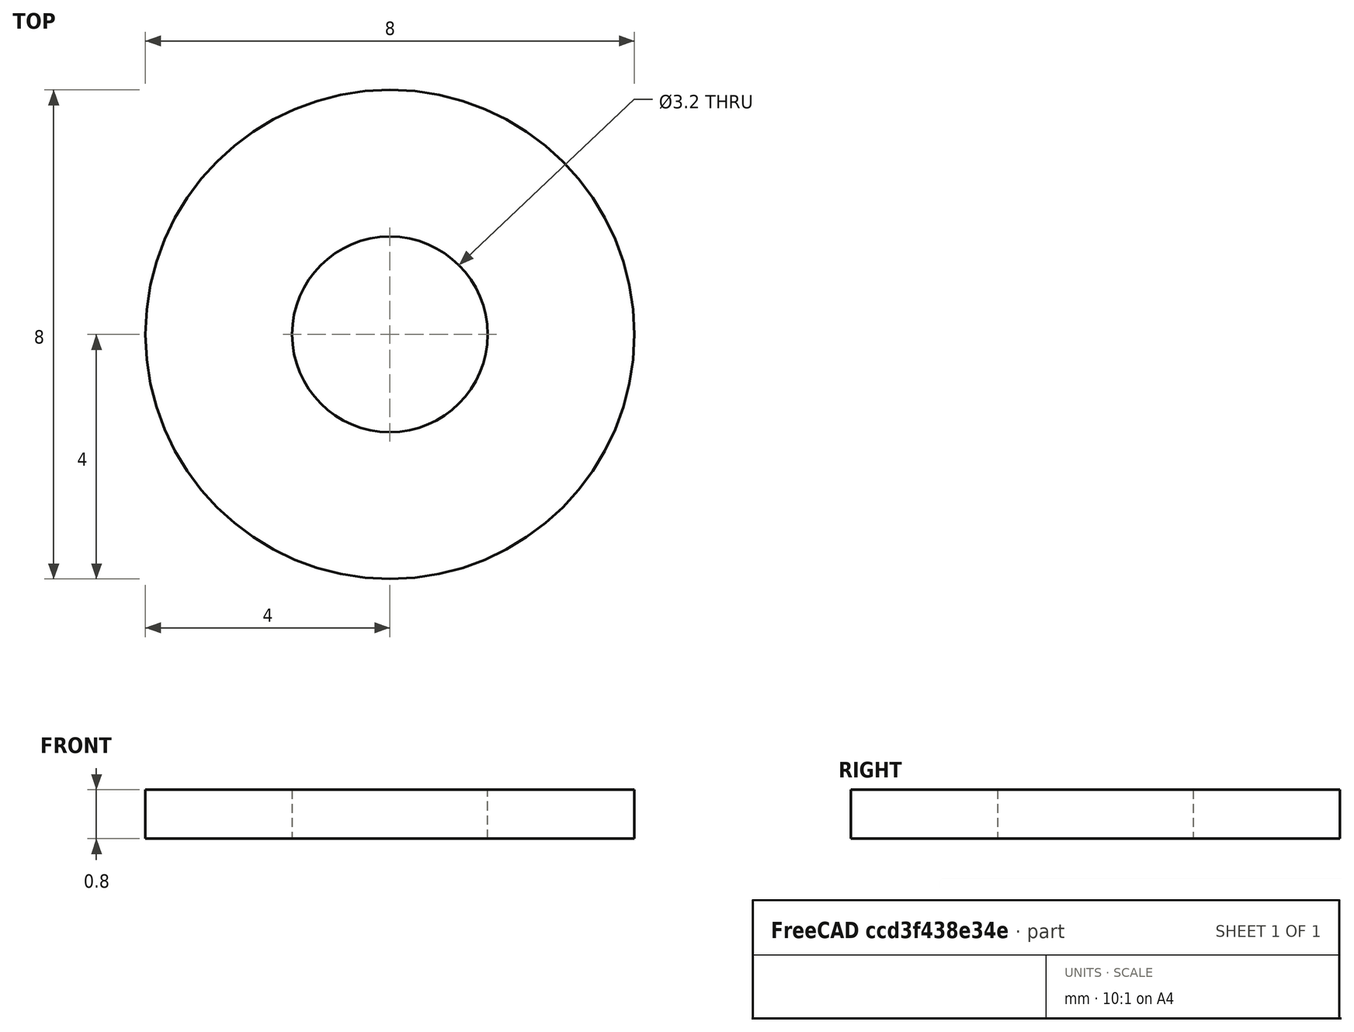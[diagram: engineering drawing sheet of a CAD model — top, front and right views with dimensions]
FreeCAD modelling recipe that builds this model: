
FCSTD DOCUMENT  (FreeCAD 1.0R39319 (Git))
Label: rondelleM3
License: All rights reserved
LicenseURL: https://en.wikipedia.org/wiki/All_rights_reserved
objects: Sketcher::SketchObject×1, PartDesign::Pad×1, PartDesign::Body×1
note: 6 computed .brp shape members not serialized (recipe doc carries the construction recipe); baked Part::Feature solids carry a one-line shape summary decoded from their .brp

FEATURE [Sketcher::SketchObject] Sketch
  ArcFitTolerance = 1e-06
  AttachmentSupport = -> [XY_Plane]
  FullyConstrained = true
  MakeInternals = false
  MapMode = 5
  sketch-geometry (2):
    g0: Circle CenterX=0 CenterY=0 CenterZ=0 NormalX=0 NormalY=0 NormalZ=1 AngleXU=0 Radius=1.6
    g1: Circle CenterX=0 CenterY=0 CenterZ=0 NormalX=0 NormalY=0 NormalZ=1 AngleXU=0 Radius=4
  constraints (4):
    c: Coincident(g0,g-1)
    c: Coincident(g1,g0)
    c: Diameter(g0) = 3.2
    c: Diameter(g1) = 8
FEATURE [PartDesign::Pad] Pad
  Direction = (0,0,1)
  Length = 0.8
  Length2 = 10
  Profile = -> Sketch
  ReferenceAxis = -> Sketch [N_Axis]
  Refine = true
  Suppressed = false
  Type = 0
FEATURE [PartDesign::Body] Body  label="Corps"
  AllowCompound = false
  Group = -> [Sketch,Pad]
  Origin = -> Origin
  Tip = -> Pad
